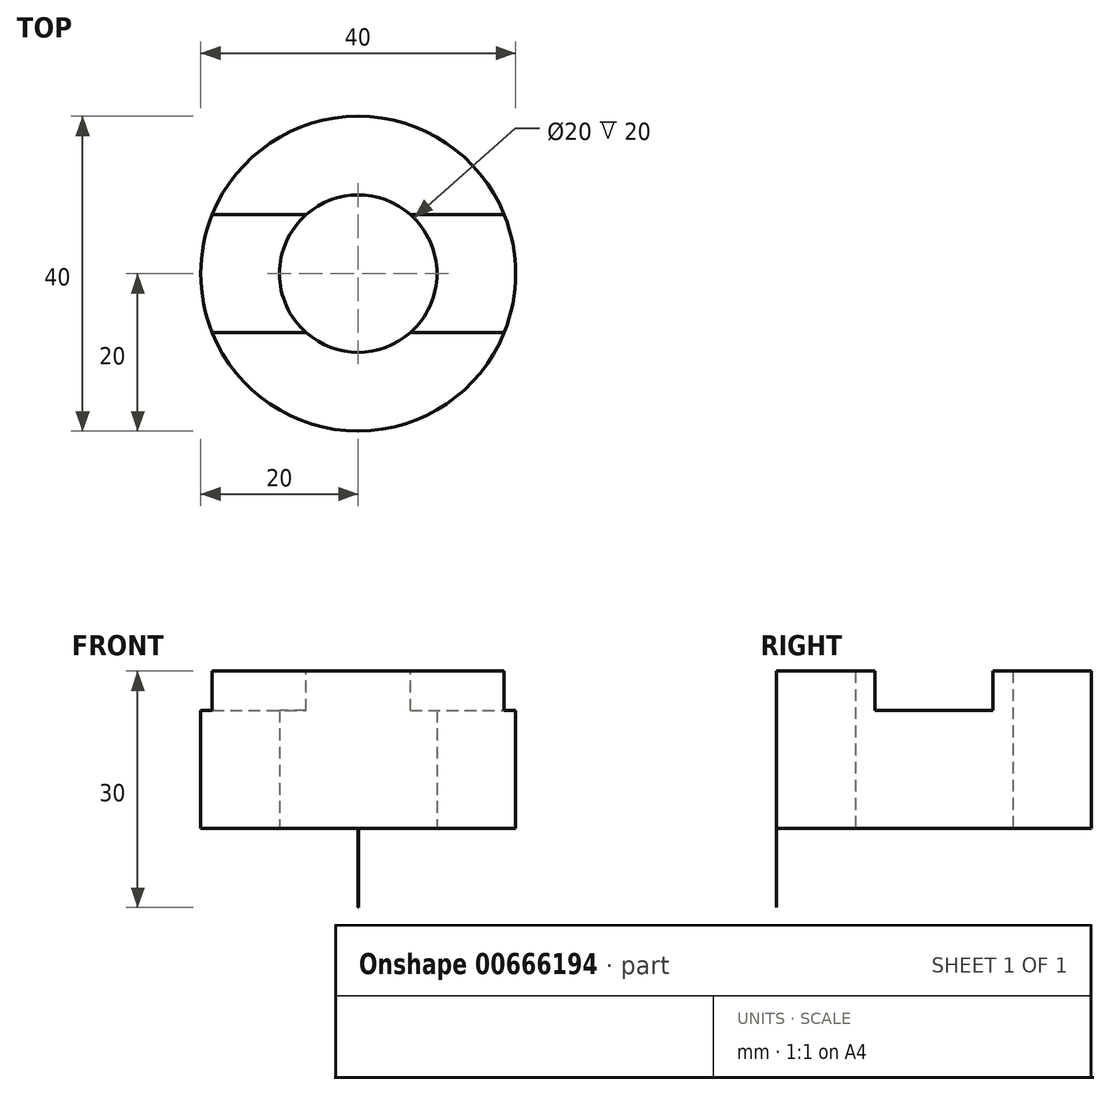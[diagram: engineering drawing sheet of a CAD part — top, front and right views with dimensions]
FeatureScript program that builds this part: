
annotation { "Feature Type Name" : "Feature", "Feature Type Description" : "" }
export const myFeature = defineFeature(function(context is Context, id is Id, definition is map)
    precondition{}
    {
        {
            var Q0;
            Q0=qCreatedBy(makeId("Top.planeOp"),FACE);
            var sketch = newSketch(context, id + "F0", { "sketchPlane" : qUnion([Q0])});
            skArc(sketch, "E0", {"start": v(0, 20) * mm, "mid": v(-20, -0.03) * mm, "end": v(0.06, -20) * mm});
            skArc(sketch, "E1", {"start": v(49.7, -19.92) * mm, "mid": v(71.42, -0.87) * mm, "end": v(51.44, 20) * mm});
            skLineSegment(sketch, "E2", {"start": v(0, 20) * mm, "end": v(51.44, 20) * mm});
            skLineSegment(sketch, "E3", {"start": v(0, -20) * mm, "end": v(53.25, -19.92) * mm});
            skSolve(sketch);
        }
        {
            var Q0;
            {var subQ1=sQuery(id+"F0.wireOp",EDGE,"E0");Q0=makeQuery(id+"F0.imprint","IMPRINT",FACE,{"disambiguationData":[TD([[makeQuery(id+"F0.imprint","IMPRINT",EDGE,{"derivedFrom":subQ1}),1.0]])]});}
            extrude(context, id + "F1", {"entities" : qUnion([Q0]), "depth" : 10 * mm, "offsetDistance" : 25 * mm});
        }
        {
            var Q0;
            Q0=makeQuery(id+"F1.opExtrude","CAP_FACE",FACE,{"disambiguationData":[OSD([sQuery(id+"F0.wireOp",EDGE,"E0"),sQuery(id+"F0.wireOp",EDGE,"E1"),sQuery(id+"F0.wireOp",EDGE,"E2"),sQuery(id+"F0.wireOp",EDGE,"E3")])],"isStart":false});
            var sketch = newSketch(context, id + "F2", { "sketchPlane" : qUnion([Q0])});
            skCircle(sketch, "E4", {"center": v(0, 0) * mm, "radius": 20 * mm});
            skCircle(sketch, "E5", {"center": v(0, 0) * mm, "radius": 10 * mm});
            skSolve(sketch);
        }
        {
            var Q0;
            Q0=makeQuery(id+"F2.imprint","IMPRINT",FACE,{"disambiguationData":[TD([[makeQuery(id+"F2.imprint","IMPRINT",EDGE,{"derivedFrom":sQuery(id+"F2.wireOp",EDGE,"E5")}),-1.0]])]});
            extrude(context, id + "F3", {"entities" : qUnion([Q0]), "operationType" : NewBodyOperationType.ADD, "depth" : 20 * mm, "offsetDistance" : 25 * mm});
        }
        {
            var Q0;
            Q0=makeQuery(id+"F3.opExtrude","CAP_FACE",FACE,{"disambiguationData":[OSD([sQuery(id+"F2.wireOp",EDGE,"E4"),sQuery(id+"F2.wireOp",EDGE,"E5")])],"isStart":false});
            var sketch = newSketch(context, id + "F4", { "sketchPlane" : qUnion([Q0])});
            skLineSegment(sketch, "E6", {"start": v(-18.54, 7.5) * mm, "end": v(18.54, 7.5) * mm});
            skLineSegment(sketch, "E7", {"start": v(-18.54, -7.5) * mm, "end": v(18.54, -7.5) * mm});
            skSolve(sketch);
        }
        {
            var Q0;
            {var subQ0=sQuery(id+"F4.wireOp",EDGE,"E6");var subQ5=makeQuery(id+"F3.opExtrude","CAP_EDGE",EDGE,{"disambiguationData":[OSD([sQuery(id+"F2.wireOp",EDGE,"E5")])],"isStart":false});var subQ6=makeQuery(id+"F4.imprint","INTERSECT",VERTEX,{"disambiguationData":[OD(0.0)],"derivedFrom":[subQ5,subQ0]});Q0=makeQuery(id+"F4.imprint","IMPRINT",FACE,{"disambiguationData":[TD([[makeQuery(id+"F4.imprint","IMPRINT",EDGE,{"disambiguationData":[TD([[subQ6,-1.0]])],"derivedFrom":subQ5}),-1.0]])]});}
            var Q1;
            {var subQ0=sQuery(id+"F4.wireOp",EDGE,"E6");var subQ5=makeQuery(id+"F3.opExtrude","CAP_EDGE",EDGE,{"disambiguationData":[OSD([sQuery(id+"F2.wireOp",EDGE,"E5")])],"isStart":false});var subQ6=makeQuery(id+"F4.imprint","INTERSECT",VERTEX,{"disambiguationData":[OD(1.0)],"derivedFrom":[subQ5,subQ0]});Q1=makeQuery(id+"F4.imprint","IMPRINT",FACE,{"disambiguationData":[TD([[makeQuery(id+"F4.imprint","IMPRINT",EDGE,{"disambiguationData":[TD([[subQ6,1.0]])],"derivedFrom":subQ5}),-1.0]])]});}
            extrude(context, id + "F5", {"entities" : qUnion([Q0, Q1]), "operationType" : NewBodyOperationType.REMOVE, "oppositeDirection" : true, "depth" : 5 * mm, "offsetDistance" : 25 * mm});
        }
    });
